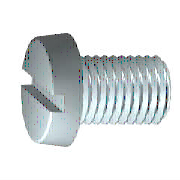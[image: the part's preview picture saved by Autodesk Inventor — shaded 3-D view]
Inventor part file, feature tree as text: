
AUTODESK INVENTOR PART (.ipt)
format: ipt  version: 2015 (Build 190159000, 159)  size: 189,440 bytes
history: native  units: mm (DEFAULTED — no unit token found)
features: sketch x2, other x1, extrude x1, plane x1
ambient origin geometry x7: Origin, YZ Plane, XZ Plane, X Axis, Y Axis, Z Axis, Center Point
bodies: Body1 (feature_tree)
feature tree (5):
  other  "Bryła"
  sketch  "Szkic2"
  extrude  "Szczelina"  Depth=12.0mm
  plane  "Work Plane1"
  sketch  "Szkic1"
